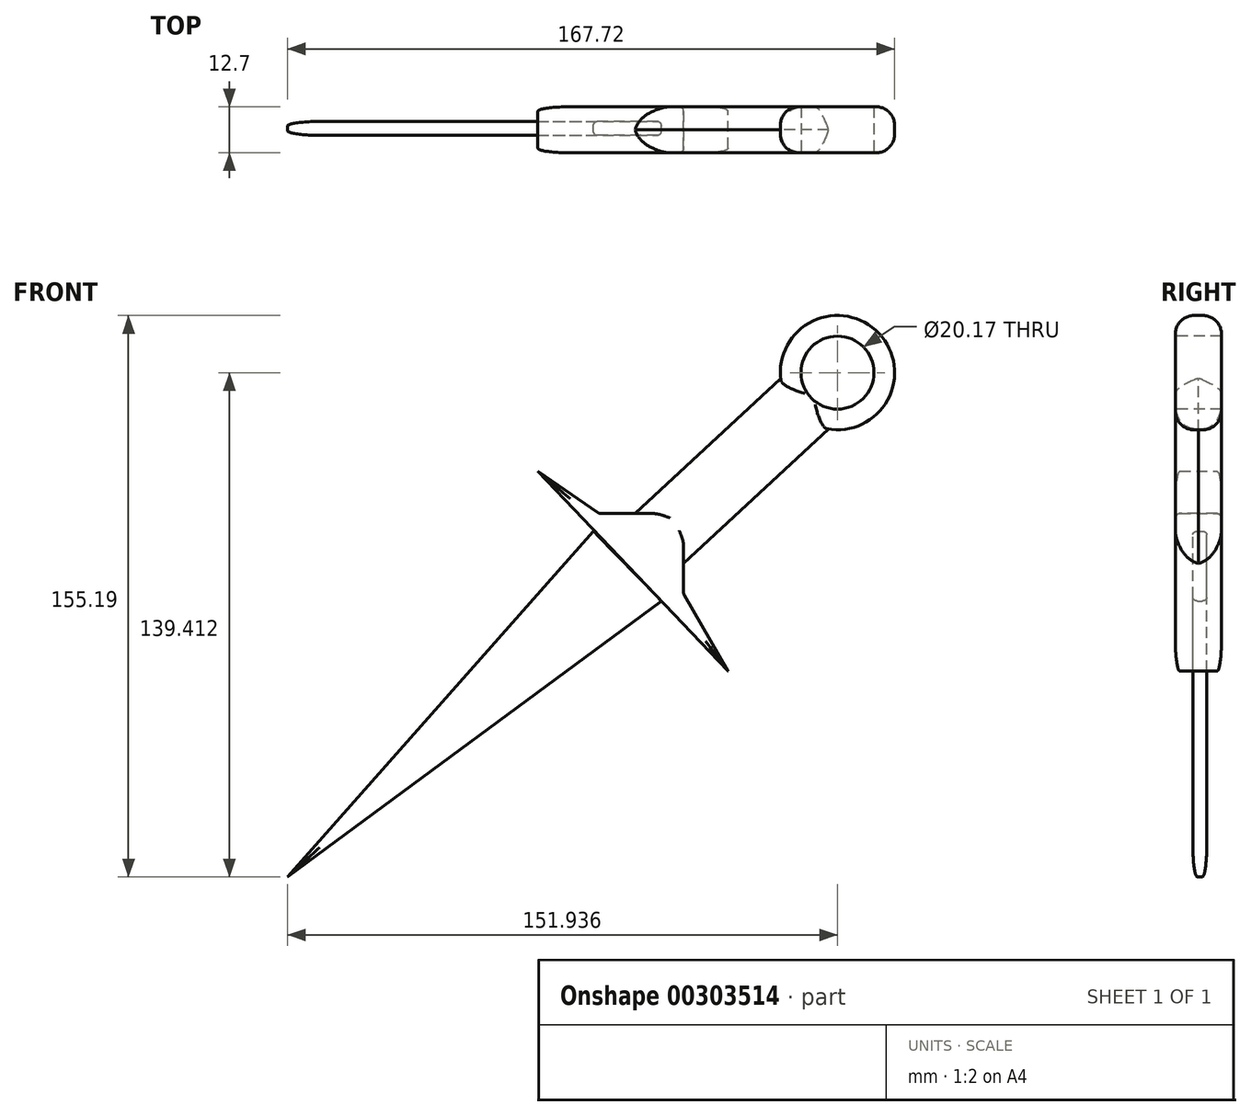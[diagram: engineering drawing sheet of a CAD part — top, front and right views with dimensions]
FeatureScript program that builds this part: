
annotation { "Feature Type Name" : "Feature", "Feature Type Description" : "" }
export const myFeature = defineFeature(function(context is Context, id is Id, definition is map)
    precondition{}
    {
        {
            var Q0;
            Q0=qCreatedBy(makeId("Front.planeOp"),FACE);
            var sketch = newSketch(context, id + "F0", { "sketchPlane" : qUnion([Q0])});
            skLineSegment(sketch, "E0", {"start": v(-3.82, 69.88) * mm, "end": v(48.7, 14.67) * mm});
            skLineSegment(sketch, "E1", {"start": v(-3.82, 69.88) * mm, "end": v(13.21, 58.2) * mm});
            skLineSegment(sketch, "E2", {"start": v(13.21, 58.2) * mm, "end": v(22.9, 58.2) * mm});
            skLineSegment(sketch, "E3", {"start": v(48.7, 14.67) * mm, "end": v(36.45, 35.97) * mm});
            skLineSegment(sketch, "E4", {"start": v(36.45, 35.97) * mm, "end": v(36.45, 44.28) * mm});
            skLineSegment(sketch, "E5", {"start": v(22.9, 58.2) * mm, "end": v(64.85, 97.16) * mm});
            skLineSegment(sketch, "E6", {"start": v(36.45, 44.28) * mm, "end": v(78.94, 83.72) * mm});
            skCircle(sketch, "E7", {"center": v(78.94, 97.16) * mm, "radius": 15.78 * mm});
            skSolve(sketch);
        }
        {
            var Q0;
            Q0 = qSketchRegion(id + "F0", true);
            extrude(context, id + "F1", {"entities" : qUnion([Q0]), "depth" : 12.7 * mm});
        }
        {
            var Q0;
            Q0=qCreatedBy(makeId("Front.planeOp"),FACE);
            var sketch = newSketch(context, id + "F2", { "sketchPlane" : qUnion([Q0])});
            skLineSegment(sketch, "E8", {"start": v(-73, -42.25) * mm, "end": v(30.25, 34.04) * mm});
            skLineSegment(sketch, "E9", {"start": v(-73, -42.25) * mm, "end": v(11.53, 53.34) * mm});
            skLineSegment(sketch, "E10", {"start": v(30.25, 34.04) * mm, "end": v(11.53, 53.34) * mm});
            skSolve(sketch);
        }
        {
            var Q0;
            Q0 = qSketchRegion(id + "F2", true);
            extrude(context, id + "F3", {"entities" : qUnion([Q0]), "depth" : 7.87 * mm, "hasSecondDirection" : true, "secondDirectionOppositeDirection" : false, "secondDirectionDepth" : 4.06 * mm});
        }
        {
            var Q0;
            Q0=makeQuery(id+"F1.opExtrude","CAP_EDGE",EDGE,{"disambiguationData":[OSD([sQuery(id+"F0.wireOp",EDGE,"E5")])],"isStart":false});
            var Q1;
            Q1=makeQuery(id+"F1.opExtrude","CAP_EDGE",EDGE,{"disambiguationData":[OSD([sQuery(id+"F0.wireOp",EDGE,"E5")])],"isStart":true});
            var Q2;
            Q2=makeQuery(id+"F1.opExtrude","CAP_EDGE",EDGE,{"disambiguationData":[OSD([sQuery(id+"F0.wireOp",EDGE,"E6")])],"isStart":false});
            var Q3;
            Q3=makeQuery(id+"F1.opExtrude","CAP_EDGE",EDGE,{"disambiguationData":[OSD([sQuery(id+"F0.wireOp",EDGE,"E6")])],"isStart":true});
            fillet(context, id + "F4", {"entities" : qUnion([Q0, Q1, Q2, Q3]), "radius" : 7.62 * mm, "tangentPropagation" : true, "allowEdgeOverflow" : false});
        }
        {
            var Q0;
            Q0=makeQuery(id+"F1.opExtrude","CAP_EDGE",EDGE,{"disambiguationData":[OSD([sQuery(id+"F0.wireOp",EDGE,"E7")])],"isStart":true});
            var Q1;
            Q1=makeQuery(id+"F1.opExtrude","CAP_EDGE",EDGE,{"disambiguationData":[OSD([sQuery(id+"F0.wireOp",EDGE,"E7")])],"isStart":false});
            fillet(context, id + "F5", {"entities" : qUnion([Q0, Q1]), "radius" : 5.08 * mm, "tangentPropagation" : true, "allowEdgeOverflow" : false});
        }
        {
            var Q0;
            Q0=makeQuery(id+"F1.opExtrude","CAP_EDGE",EDGE,{"disambiguationData":[OSD([sQuery(id+"F0.wireOp",EDGE,"E1")])],"isStart":true});
            var Q1;
            Q1=makeQuery(id+"F1.opExtrude","CAP_EDGE",EDGE,{"disambiguationData":[OSD([sQuery(id+"F0.wireOp",EDGE,"E2")])],"isStart":true});
            var Q2;
            Q2=makeQuery(id+"F1.opExtrude","CAP_EDGE",EDGE,{"disambiguationData":[OSD([sQuery(id+"F0.wireOp",EDGE,"E1")])],"isStart":false});
            var Q3;
            Q3=makeQuery(id+"F1.opExtrude","CAP_EDGE",EDGE,{"disambiguationData":[OSD([sQuery(id+"F0.wireOp",EDGE,"E2")])],"isStart":false});
            var Q4;
            Q4=makeQuery(id+"F1.opExtrude","CAP_EDGE",EDGE,{"disambiguationData":[OSD([sQuery(id+"F0.wireOp",EDGE,"E4")])],"isStart":true});
            var Q5;
            Q5=makeQuery(id+"F1.opExtrude","CAP_EDGE",EDGE,{"disambiguationData":[OSD([sQuery(id+"F0.wireOp",EDGE,"E3")])],"isStart":true});
            var Q6;
            Q6=makeQuery(id+"F1.opExtrude","CAP_EDGE",EDGE,{"disambiguationData":[OSD([sQuery(id+"F0.wireOp",EDGE,"E4")])],"isStart":false});
            var Q7;
            Q7=makeQuery(id+"F1.opExtrude","CAP_EDGE",EDGE,{"disambiguationData":[OSD([sQuery(id+"F0.wireOp",EDGE,"E3")])],"isStart":false});
            var Q8;
            Q8=makeQuery(id+"F1.opExtrude","SWEPT_EDGE",EDGE,{"disambiguationData":[OSD([sQuery(id+"F0.wireOp",EDGE,"E3"),sQuery(id+"F0.wireOp",EDGE,"E4")])]});
            var Q9;
            Q9=makeQuery(id+"F1.opExtrude","SWEPT_EDGE",EDGE,{"disambiguationData":[OSD([sQuery(id+"F0.wireOp",EDGE,"E1"),sQuery(id+"F0.wireOp",EDGE,"E2")])]});
            var Q10;
            Q10=makeQuery(id+"F1.opExtrude","CAP_EDGE",EDGE,{"disambiguationData":[OSD([sQuery(id+"F0.wireOp",EDGE,"E0")])],"isStart":true});
            var Q11;
            Q11=makeQuery(id+"F1.opExtrude","CAP_EDGE",EDGE,{"disambiguationData":[OSD([sQuery(id+"F0.wireOp",EDGE,"E0")])],"isStart":false});
            fillet(context, id + "F6", {"entities" : qUnion([Q0, Q1, Q2, Q3, Q4, Q5, Q6, Q7, Q8, Q9, Q10, Q11]), "radius" : 1.23 * mm, "tangentPropagation" : true, "allowEdgeOverflow" : false});
        }
        {
            var Q0;
            Q0=makeQuery(id+"F3.opExtrude","CAP_EDGE",EDGE,{"disambiguationData":[OSD([sQuery(id+"F2.wireOp",EDGE,"E8")])],"isStart":false});
            var Q1;
            Q1=makeQuery(id+"F3.opExtrude","CAP_EDGE",EDGE,{"disambiguationData":[OSD([sQuery(id+"F2.wireOp",EDGE,"E9")])],"isStart":false});
            fillet(context, id + "F7", {"entities" : qUnion([Q0, Q1]), "radius" : 1.27 * mm, "tangentPropagation" : true, "allowEdgeOverflow" : false});
        }
        {
            var Q0;
            Q0=makeQuery(id+"F3.opExtrude","CAP_EDGE",EDGE,{"disambiguationData":[OSD([sQuery(id+"F2.wireOp",EDGE,"E9")])],"isStart":true});
            var Q1;
            Q1=makeQuery(id+"F3.opExtrude","CAP_EDGE",EDGE,{"disambiguationData":[OSD([sQuery(id+"F2.wireOp",EDGE,"E8")])],"isStart":true});
            fillet(context, id + "F8", {"entities" : qUnion([Q0, Q1]), "radius" : 1.27 * mm, "tangentPropagation" : true, "allowEdgeOverflow" : false});
        }
        {
            var Q0;
            Q0=makeQuery(id+"F1.opExtrude","CAP_FACE",FACE,{"disambiguationData":[OSD([sQuery(id+"F0.wireOp",EDGE,"E0"),sQuery(id+"F0.wireOp",EDGE,"E1"),sQuery(id+"F0.wireOp",EDGE,"E2"),sQuery(id+"F0.wireOp",EDGE,"E3"),sQuery(id+"F0.wireOp",EDGE,"E4"),sQuery(id+"F0.wireOp",EDGE,"E5"),sQuery(id+"F0.wireOp",EDGE,"E6"),sQuery(id+"F0.wireOp",EDGE,"E7")])],"isStart":false});
            var sketch = newSketch(context, id + "F9", { "sketchPlane" : qUnion([Q0])});
            skCircle(sketch, "E11", {"center": v(78.94, 97.16) * mm, "radius": 10.08 * mm});
            skSolve(sketch);
        }
        {
            var Q0;
            Q0 = qSketchRegion(id + "F9", true);
            extrude(context, id + "F10", {"entities" : qUnion([Q0]), "operationType" : NewBodyOperationType.REMOVE, "oppositeDirection" : true, "depth" : 12.7 * mm});
        }
    });
